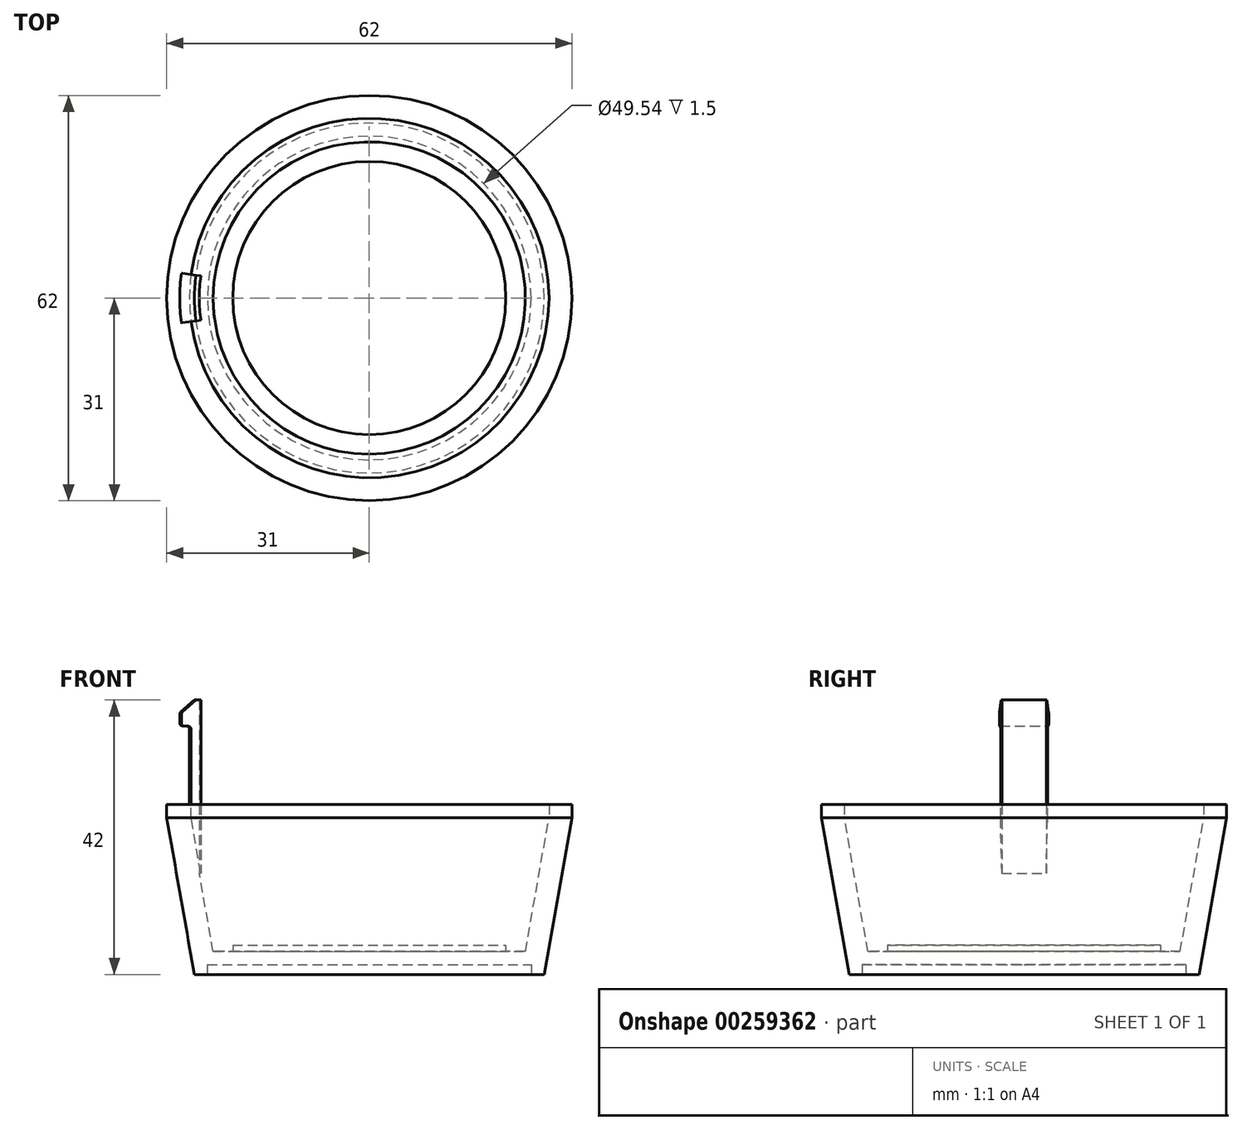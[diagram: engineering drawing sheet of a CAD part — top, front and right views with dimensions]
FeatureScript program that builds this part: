
annotation { "Feature Type Name" : "Feature", "Feature Type Description" : "" }
export const myFeature = defineFeature(function(context is Context, id is Id, definition is map)
    precondition{}
    {
        {
            var Q0;
            Q0=qCreatedBy(makeId("Front.planeOp"),FACE);
            var sketch = newSketch(context, id + "F0", { "sketchPlane" : qUnion([Q0])});
            skLineSegment(sketch, "E0", {"start": v(0, 0) * mm, "end": v(0, 50) * mm, "construction": true});
            skLineSegment(sketch, "E1", {"start": v(0, 1.5) * mm, "end": v(-24.77, 1.5) * mm});
            skLineSegment(sketch, "E2", {"start": v(-24.77, 1.5) * mm, "end": v(-24.77, 0) * mm});
            skLineSegment(sketch, "E3", {"start": v(-24.77, 0) * mm, "end": v(-26.77, 0) * mm});
            skLineSegment(sketch, "E4", {"start": v(-26.77, 0) * mm, "end": v(-31, 24) * mm});
            skLineSegment(sketch, "E5", {"start": v(-23.89, 3.5) * mm, "end": v(-20.89, 3.5) * mm});
            skLineSegment(sketch, "E6", {"start": v(-20.89, 3.5) * mm, "end": v(-20.89, 4.5) * mm});
            skLineSegment(sketch, "E7", {"start": v(-20.89, 4.5) * mm, "end": v(0, 4.5) * mm});
            skLineSegment(sketch, "E8", {"start": v(0, 4.5) * mm, "end": v(0, 1.5) * mm});
            skLineSegment(sketch, "E9", {"start": v(-31, 26) * mm, "end": v(-27.5, 26) * mm});
            skLineSegment(sketch, "E10", {"start": v(-31, 26) * mm, "end": v(-31, 24) * mm});
            skLineSegment(sketch, "E11", {"start": v(-27.5, 26) * mm, "end": v(-27.5, 24) * mm});
            skLineSegment(sketch, "E12", {"start": v(-27.5, 24) * mm, "end": v(-23.89, 3.5) * mm});
            skLineSegment(sketch, "E13", {"start": v(-31, 24) * mm, "end": v(-31, 0) * mm, "construction": true});
            skSolve(sketch);
        }
        {
            var Q0;
            Q0=makeQuery(id+"F0.imprint","IMPRINT",FACE,{"disambiguationData":[TD([[makeQuery(id+"F0.imprint","IMPRINT",EDGE,{"derivedFrom":sQuery(id+"F0.wireOp",EDGE,"E1")}),-1.0]])]});
            var Q1;
            Q1=sQuery(id+"F0.wireOp",EDGE,"E0");
            revolve(context, id + "F1", {"entities" : qUnion([Q0]), "axis" : qUnion([Q1]), "revolveType" : RevolveType.FULL});
        }
        {
            var Q0;
            Q0=qCreatedBy(makeId("Front.planeOp"),FACE);
            var sketch = newSketch(context, id + "F2", { "sketchPlane" : qUnion([Q0])});
            skLineSegment(sketch, "E14", {"start": v(-27.5, 24) * mm, "end": v(-27.5, 38) * mm});
            skLineSegment(sketch, "E15", {"start": v(-27.5, 38) * mm, "end": v(-29, 38) * mm});
            skLineSegment(sketch, "E16", {"start": v(-29, 38) * mm, "end": v(-29, 40) * mm});
            skLineSegment(sketch, "E17", {"start": v(-29, 40) * mm, "end": v(-26.75, 42) * mm});
            skLineSegment(sketch, "E18", {"start": v(-26.75, 42) * mm, "end": v(-26, 42) * mm});
            skLineSegment(sketch, "E19", {"start": v(-26, 42) * mm, "end": v(-26, 15.5) * mm});
            skLineSegment(sketch, "E20", {"start": v(-26, 15.5) * mm, "end": v(-27.5, 24) * mm});
            skSolve(sketch);
        }
        {
            var Q0;
            Q0=makeQuery(id+"F2.imprint","IMPRINT",FACE,{"disambiguationData":[TD([[makeQuery(id+"F2.imprint","IMPRINT",EDGE,{"derivedFrom":sQuery(id+"F2.wireOp",EDGE,"E14")}),-1.0]])]});
            var Q1;
            Q1=sQuery(id+"F0.wireOp",EDGE,"E0");
            revolve(context, id + "F3", {"operationType" : NewBodyOperationType.ADD, "entities" : qUnion([Q0]), "axis" : qUnion([Q1]), "revolveType" : RevolveType.TWO_DIRECTIONS, "angle" : 7.5 * degree, "angleBack" : 352.5 * degree});
        }
        {
            var Q0;
            Q0=makeQuery(id+"F3.opRevolve","SWEPT_EDGE",EDGE,{"disambiguationData":[OSD([sQuery(id+"F2.wireOp",EDGE,"E15"),sQuery(id+"F2.wireOp",EDGE,"E16")])]});
            var Q1;
            Q1=makeQuery(id+"F3.opRevolve","SWEPT_EDGE",EDGE,{"disambiguationData":[OSD([sQuery(id+"F2.wireOp",EDGE,"E16"),sQuery(id+"F2.wireOp",EDGE,"E17")])]});
            var Q2;
            Q2=makeQuery(id+"F3.opRevolve","SWEPT_EDGE",EDGE,{"disambiguationData":[OSD([sQuery(id+"F2.wireOp",EDGE,"E14"),sQuery(id+"F2.wireOp",EDGE,"E15")])]});
            fillet(context, id + "F4", {"entities" : qUnion([Q0, Q1, Q2]), "radius" : .5 * mm, "tangentPropagation" : true, "allowEdgeOverflow" : false});
        }
    });
